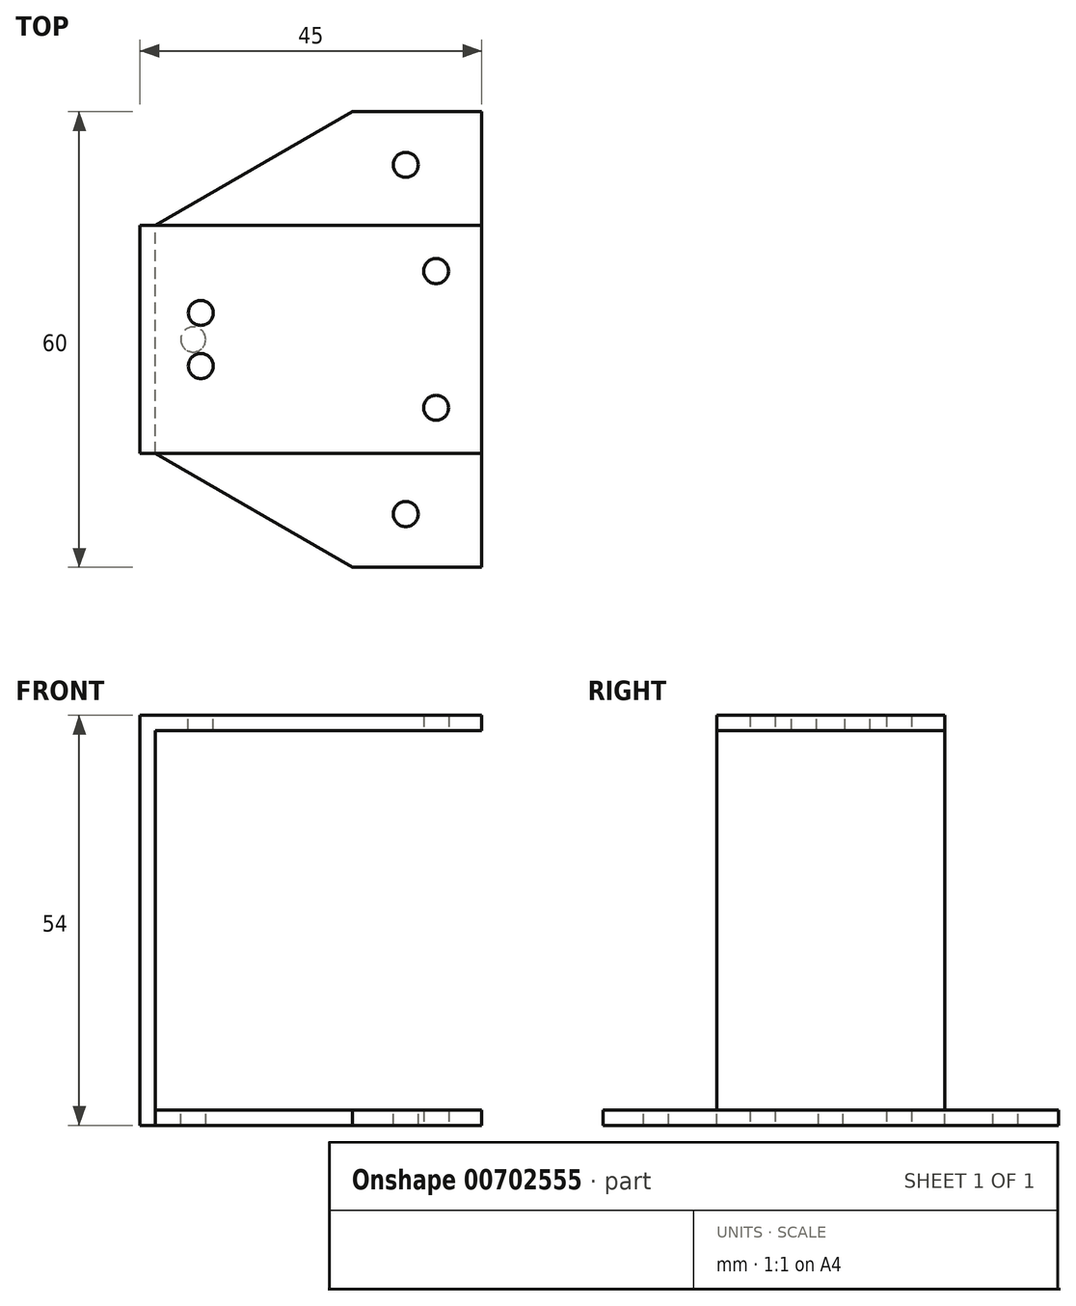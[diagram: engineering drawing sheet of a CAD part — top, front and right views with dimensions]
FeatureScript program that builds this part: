
annotation { "Feature Type Name" : "Feature", "Feature Type Description" : "" }
export const myFeature = defineFeature(function(context is Context, id is Id, definition is map)
    precondition{}
    {
        {
            var Q0;
            Q0=qCreatedBy(makeId("Front.planeOp"),FACE);
            var sketch = newSketch(context, id + "F0", { "sketchPlane" : qUnion([Q0])});
            skLineSegment(sketch, "E0", {"start": v(0, 0) * mm, "end": v(-45, 0) * mm});
            skLineSegment(sketch, "E1", {"start": v(-45, 0) * mm, "end": v(-45, 54) * mm});
            skLineSegment(sketch, "E2", {"start": v(-45, 54) * mm, "end": v(0, 54) * mm});
            skLineSegment(sketch, "E3.0", {"start": v(-43, 52) * mm, "end": v(0, 52) * mm});
            skLineSegment(sketch, "E3.1", {"start": v(-43, 2) * mm, "end": v(-43, 52) * mm});
            skLineSegment(sketch, "E3.2", {"start": v(0, 2) * mm, "end": v(-43, 2) * mm});
            skLineSegment(sketch, "E4", {"start": v(0, 52) * mm, "end": v(0, 54) * mm});
            skLineSegment(sketch, "E5", {"start": v(0, 2) * mm, "end": v(0, 0) * mm});
            skSolve(sketch);
        }
        {
            var Q0;
            Q0 = qSketchRegion(id + "F0", true);
            extrude(context, id + "F1", {"entities" : qUnion([Q0]), "endBound" : BoundingType.SYMMETRIC, "depth" : 30 * mm, "offsetDistance" : 25 * mm});
        }
        {
            var Q0;
            Q0=makeQuery(id+"F1.opExtrude","SWEPT_FACE",FACE,{"disambiguationData":[OSD([sQuery(id+"F0.wireOp",EDGE,"E0")])]});
            var sketch = newSketch(context, id + "F2", { "sketchPlane" : qUnion([Q0])});
            skLineSegment(sketch, "E6", {"start": v(0, 15) * mm, "end": v(0, -15) * mm});
            skLineSegment(sketch, "E7.0", {"start": v(-6, 0) * mm, "end": v(-6, 0) * mm});
            skLineSegment(sketch, "E8", {"start": v(0, 0) * mm, "end": v(-6, 0) * mm, "construction": true});
            skLineSegment(sketch, "E9", {"start": v(0, -9) * mm, "end": v(-18.23, -9) * mm, "construction": true});
            skCircle(sketch, "E10", {"center": v(-6, -9) * mm, "radius": 1.55 * mm});
            skLineSegment(sketch, "E11.MirrorCS", {"start": v(0, 9) * mm, "end": v(-18.23, 9) * mm, "construction": true});
            skCircle(sketch, "E12.MirrorC", {"center": v(-6, 9) * mm, "radius": 1.55 * mm});
            skSolve(sketch);
        }
        {
            var Q0;
            Q0=sQuery(id+"F2.wireOp",VERTEX,"E12.MirrorC.center");
            var Q1;
            Q1=sQuery(id+"F2.wireOp",VERTEX,"E10.center");
            var Q2;
            Q2=makeQuery(id+"F1.opExtrude","SWEPT_BODY",BODY,{"disambiguationData":[OSD([sQuery(id+"F0.wireOp",EDGE,"E0"),sQuery(id+"F0.wireOp",EDGE,"E1"),sQuery(id+"F0.wireOp",EDGE,"E2"),sQuery(id+"F0.wireOp",EDGE,"E3.0"),sQuery(id+"F0.wireOp",EDGE,"E3.1"),sQuery(id+"F0.wireOp",EDGE,"E3.2"),sQuery(id+"F0.wireOp",EDGE,"E4"),sQuery(id+"F0.wireOp",EDGE,"E5")])]});
            hole(context, id + "F3", {"style" : HoleStyle.SIMPLE, "endStyle" : HoleEndStyle.THROUGH, "standardTappedOrClearance" : lookupTablePath({ "standard" : "ISO", "fit" : "Normal", "size" : "M3", "type" : "Clearance" }), "standardBlindInLast" : lookupTablePath({ "fit" : "Standard", "standard" : "ISO", "size" : "M3", "type" : "Clearance" }), "holeDiameter" : 3.3 * mm, "majorDiameter" : 5 * mm, "isTappedThrough" : true, "tappedDepth" : 12 * mm, "tapClearance" : 3, "locations" : qUnion([Q0, Q1]), "scope" : qUnion([Q2])});
        }
        {
            var Q0;
            Q0=makeQuery(id+"F1.opExtrude","SWEPT_FACE",FACE,{"disambiguationData":[OSD([sQuery(id+"F0.wireOp",EDGE,"E2")])]});
            var sketch = newSketch(context, id + "F4", { "sketchPlane" : qUnion([Q0])});
            skLineSegment(sketch, "E13", {"start": v(-45, -15) * mm, "end": v(-45, 15) * mm});
            skLineSegment(sketch, "E14", {"start": v(-45, 0) * mm, "end": v(0, 0) * mm});
            skLineSegment(sketch, "E15", {"start": v(-45, 3.5) * mm, "end": v(-29.41, 3.5) * mm, "construction": true});
            skLineSegment(sketch, "E16", {"start": v(-37, 0) * mm, "end": v(-37, 16.87) * mm, "construction": true});
            skCircle(sketch, "E17", {"center": v(-37, 3.5) * mm, "radius": 1.55 * mm, "construction": true});
            skLineSegment(sketch, "E18.MirrorCS", {"start": v(-45, -3.5) * mm, "end": v(-29.41, -3.5) * mm, "construction": true});
            skCircle(sketch, "E19.MirrorC", {"center": v(-37, -3.5) * mm, "radius": 1.55 * mm, "construction": true});
            skLineSegment(sketch, "E20.MirrorCS", {"start": v(-37, 0) * mm, "end": v(-37, -16.87) * mm, "construction": true});
            skSolve(sketch);
        }
        {
            var Q0;
            Q0=sQuery(id+"F4.wireOp",VERTEX,"E17.center");
            var Q1;
            Q1=sQuery(id+"F4.wireOp",VERTEX,"E19.MirrorC.center");
            var Q2;
            Q2=makeQuery(id+"F1.opExtrude","SWEPT_BODY",BODY,{"disambiguationData":[OSD([sQuery(id+"F0.wireOp",EDGE,"E0"),sQuery(id+"F0.wireOp",EDGE,"E1"),sQuery(id+"F0.wireOp",EDGE,"E2"),sQuery(id+"F0.wireOp",EDGE,"E3.0"),sQuery(id+"F0.wireOp",EDGE,"E3.1"),sQuery(id+"F0.wireOp",EDGE,"E3.2"),sQuery(id+"F0.wireOp",EDGE,"E4"),sQuery(id+"F0.wireOp",EDGE,"E5")])]});
            hole(context, id + "F5", {"style" : HoleStyle.SIMPLE, "endStyle" : HoleEndStyle.BLIND, "standardTappedOrClearance" : lookupTablePath({ "standard" : "ISO", "fit" : "Normal", "size" : "M3", "type" : "Clearance" }), "standardBlindInLast" : lookupTablePath({ "fit" : "Standard", "standard" : "ISO", "size" : "M3", "type" : "Clearance" }), "holeDiameter" : 3.3 * mm, "majorDiameter" : 3 * mm, "holeDepth" : 13.5 * mm, "isTappedThrough" : true, "tappedDepth" : 12 * mm, "tapClearance" : 3, "locations" : qUnion([Q0, Q1]), "scope" : qUnion([Q2])});
        }
        {
            var Q0;
            Q0=makeQuery(id+"F1.opExtrude","SWEPT_FACE",FACE,{"disambiguationData":[OSD([sQuery(id+"F0.wireOp",EDGE,"E3.2")])]});
            var sketch = newSketch(context, id + "F6", { "sketchPlane" : qUnion([Q0])});
            skLineSegment(sketch, "E21.0", {"start": v(-38, -12.5) * mm, "end": v(-38, 12.5) * mm});
            skLineSegment(sketch, "E22", {"start": v(-43, 0) * mm, "end": v(0, 0) * mm});
            skCircle(sketch, "E23", {"center": v(-38, 0) * mm, "radius": 2.17 * mm});
            skSolve(sketch);
        }
        {
            var Q0;
            Q0=sQuery(id+"F6.wireOp",VERTEX,"E23.center");
            var Q1;
            Q1=makeQuery(id+"F1.opExtrude","SWEPT_BODY",BODY,{"disambiguationData":[OSD([sQuery(id+"F0.wireOp",EDGE,"E0"),sQuery(id+"F0.wireOp",EDGE,"E1"),sQuery(id+"F0.wireOp",EDGE,"E2"),sQuery(id+"F0.wireOp",EDGE,"E3.0"),sQuery(id+"F0.wireOp",EDGE,"E3.1"),sQuery(id+"F0.wireOp",EDGE,"E3.2"),sQuery(id+"F0.wireOp",EDGE,"E4"),sQuery(id+"F0.wireOp",EDGE,"E5")])]});
            hole(context, id + "F7", {"style" : HoleStyle.SIMPLE, "endStyle" : HoleEndStyle.BLIND, "standardTappedOrClearance" : lookupTablePath({ "standard" : "ISO", "fit" : "Normal", "size" : "M3", "type" : "Clearance" }), "standardBlindInLast" : lookupTablePath({ "fit" : "Standard", "standard" : "ISO", "size" : "M3", "type" : "Clearance" }), "holeDiameter" : 3.3 * mm, "majorDiameter" : 5 * mm, "holeDepth" : 13.5 * mm, "isTappedThrough" : true, "tappedDepth" : 12 * mm, "tapClearance" : 3, "locations" : qUnion([Q0]), "scope" : qUnion([Q1])});
        }
        {
            var Q0;
            Q0=makeQuery(id+"F1.opExtrude","SWEPT_FACE",FACE,{"disambiguationData":[OSD([sQuery(id+"F0.wireOp",EDGE,"E3.2")])]});
            var sketch = newSketch(context, id + "F8", { "sketchPlane" : qUnion([Q0])});
            skLineSegment(sketch, "E24", {"start": v(0, -15) * mm, "end": v(0, -30) * mm});
            skLineSegment(sketch, "E25", {"start": v(0, -30) * mm, "end": v(-17, -30) * mm});
            skLineSegment(sketch, "E26", {"start": v(-17, -30) * mm, "end": v(-43, -15) * mm});
            skLineSegment(sketch, "E27", {"start": v(-43, -15) * mm, "end": v(0, -15) * mm});
            skLineSegment(sketch, "E28", {"start": v(-43, 0) * mm, "end": v(0, 0) * mm});
            skLineSegment(sketch, "E29.MirrorCS", {"start": v(-43, 15) * mm, "end": v(0, 15) * mm});
            skLineSegment(sketch, "E30.MirrorCS", {"start": v(-17, 30) * mm, "end": v(-43, 15) * mm});
            skLineSegment(sketch, "E31.MirrorCS", {"start": v(0, 30) * mm, "end": v(-17, 30) * mm});
            skLineSegment(sketch, "E32.MirrorCS", {"start": v(0, 15) * mm, "end": v(0, 30) * mm});
            skSolve(sketch);
        }
        {
            var Q0;
            Q0 = qSketchRegion(id + "F8", true);
            extrude(context, id + "F9", {"entities" : qUnion([Q0]), "oppositeDirection" : true, "depth" : 2 * mm, "offsetDistance" : 25 * mm});
        }
        {
            var Q0;
            Q0=makeQuery(id+"F1.opExtrude","SWEPT_BODY",BODY,{"disambiguationData":[OSD([sQuery(id+"F0.wireOp",EDGE,"E0"),sQuery(id+"F0.wireOp",EDGE,"E1"),sQuery(id+"F0.wireOp",EDGE,"E2"),sQuery(id+"F0.wireOp",EDGE,"E3.0"),sQuery(id+"F0.wireOp",EDGE,"E3.1"),sQuery(id+"F0.wireOp",EDGE,"E3.2"),sQuery(id+"F0.wireOp",EDGE,"E4"),sQuery(id+"F0.wireOp",EDGE,"E5")])]});
            var Q1;
            Q1=makeQuery(id+"F9.opExtrude","SWEPT_BODY",BODY,{"disambiguationData":[OSD([sQuery(id+"F8.wireOp",EDGE,"E24"),sQuery(id+"F8.wireOp",EDGE,"E25"),sQuery(id+"F8.wireOp",EDGE,"E26"),sQuery(id+"F8.wireOp",EDGE,"E27")])]});
            var Q2;
            Q2=makeQuery(id+"F9.opExtrude","SWEPT_BODY",BODY,{"disambiguationData":[OSD([sQuery(id+"F8.wireOp",EDGE,"E29.MirrorCS"),sQuery(id+"F8.wireOp",EDGE,"E30.MirrorCS"),sQuery(id+"F8.wireOp",EDGE,"E31.MirrorCS"),sQuery(id+"F8.wireOp",EDGE,"E32.MirrorCS")])]});
            booleanBodies(context, id + "F10", {"operationType" : BooleanOperationType.UNION, "tools" : qUnion([Q0, Q1, Q2])});
        }
        {
            var Q0;
            Q0=makeQuery(id+"F10.opBoolean","MERGE",FACE,{"derivedFrom":[makeQuery(id+"F1.opExtrude","SWEPT_FACE",FACE,{"disambiguationData":[OSD([sQuery(id+"F0.wireOp",EDGE,"E3.2")])]}),makeQuery(id+"F9.opExtrude","CAP_FACE",FACE,{"disambiguationData":[OSD([sQuery(id+"F8.wireOp",EDGE,"E24"),sQuery(id+"F8.wireOp",EDGE,"E25"),sQuery(id+"F8.wireOp",EDGE,"E26"),sQuery(id+"F8.wireOp",EDGE,"E27")])],"isStart":true}),makeQuery(id+"F9.opExtrude","CAP_FACE",FACE,{"disambiguationData":[OSD([sQuery(id+"F8.wireOp",EDGE,"E29.MirrorCS"),sQuery(id+"F8.wireOp",EDGE,"E30.MirrorCS"),sQuery(id+"F8.wireOp",EDGE,"E31.MirrorCS"),sQuery(id+"F8.wireOp",EDGE,"E32.MirrorCS")])],"isStart":true})]});
            var sketch = newSketch(context, id + "F11", { "sketchPlane" : qUnion([Q0])});
            skLineSegment(sketch, "E33", {"start": v(-43, 0) * mm, "end": v(0, 0) * mm});
            skLineSegment(sketch, "E34.0", {"start": v(-43, -23) * mm, "end": v(0, -23) * mm});
            skLineSegment(sketch, "E35.0", {"start": v(-10, -30) * mm, "end": v(-10, 30) * mm});
            skCircle(sketch, "E36", {"center": v(-10, -23) * mm, "radius": 2.17 * mm});
            skCircle(sketch, "E37.MirrorC", {"center": v(-10, 23) * mm, "radius": 2.17 * mm});
            skLineSegment(sketch, "E38", {"start": v(-38, 0) * mm, "end": v(-38, -23) * mm});
            skSolve(sketch);
        }
        {
            var Q0;
            Q0=sQuery(id+"F11.wireOp",VERTEX,"E37.MirrorC.center");
            var Q1;
            Q1=sQuery(id+"F11.wireOp",VERTEX,"E36.center");
            var Q2;
            Q2=makeQuery(id+"F1.opExtrude","SWEPT_BODY",BODY,{"disambiguationData":[OSD([sQuery(id+"F0.wireOp",EDGE,"E0"),sQuery(id+"F0.wireOp",EDGE,"E1"),sQuery(id+"F0.wireOp",EDGE,"E2"),sQuery(id+"F0.wireOp",EDGE,"E3.0"),sQuery(id+"F0.wireOp",EDGE,"E3.1"),sQuery(id+"F0.wireOp",EDGE,"E3.2"),sQuery(id+"F0.wireOp",EDGE,"E4"),sQuery(id+"F0.wireOp",EDGE,"E5")])]});
            hole(context, id + "F12", {"style" : HoleStyle.SIMPLE, "endStyle" : HoleEndStyle.BLIND, "standardTappedOrClearance" : lookupTablePath({ "standard" : "ISO", "fit" : "Normal", "size" : "M3", "type" : "Clearance" }), "standardBlindInLast" : lookupTablePath({ "fit" : "Standard", "standard" : "ISO", "size" : "M3", "type" : "Clearance" }), "holeDiameter" : 3.3 * mm, "majorDiameter" : 5 * mm, "holeDepth" : 13.5 * mm, "isTappedThrough" : true, "tappedDepth" : 12 * mm, "tapClearance" : 3, "locations" : qUnion([Q0, Q1]), "scope" : qUnion([Q2])});
        }
    });
